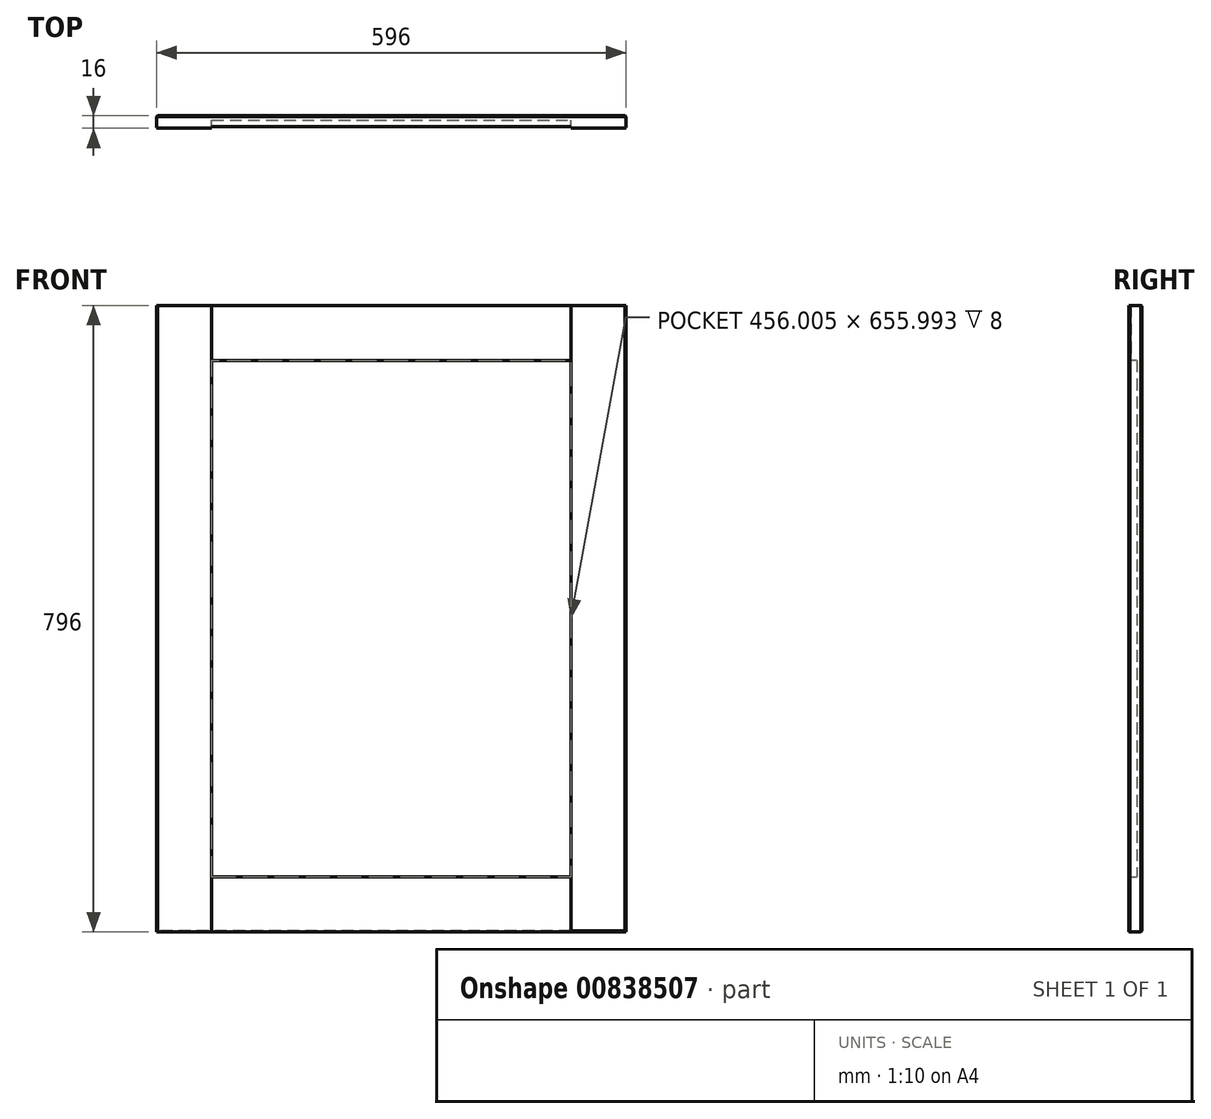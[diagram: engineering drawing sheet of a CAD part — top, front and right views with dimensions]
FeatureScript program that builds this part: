
annotation { "Feature Type Name" : "Feature", "Feature Type Description" : "" }
export const myFeature = defineFeature(function(context is Context, id is Id, definition is map)
    precondition{}
    {
        {
            var Q0;
            Q0=qCreatedBy(makeId("Front.planeOp"),FACE);
            var sketch = newSketch(context, id + "F0", { "sketchPlane" : qUnion([Q0])});
            skLineSegment(sketch, "E0.bottom", {"start": v(0, 0) * mm, "end": v(35.9, 0) * mm});
            skLineSegment(sketch, "E0.top", {"start": v(0, 30.12) * mm, "end": v(35.9, 30.12) * mm});
            skLineSegment(sketch, "E0.left", {"start": v(0, 0) * mm, "end": v(0, 30.12) * mm});
            skLineSegment(sketch, "E0.right", {"start": v(35.9, 0) * mm, "end": v(35.9, 30.12) * mm});
            skSolve(sketch);
        }
        {
            var Q0;
            Q0=makeQuery(id+"F0.imprint","IMPRINT",FACE,{"disambiguationData":[TD([[makeQuery(id+"F0.imprint","IMPRINT",EDGE,{"derivedFrom":sQuery(id+"F0.wireOp",EDGE,"E0.bottom")}),1.0]])]});
            extrude(context, id + "F1", {"entities" : qUnion([Q0]), "depth" : 16 * mm, "offsetDistance" : 25.4 * mm});
        }
        {
            var Q0;
            Q0=makeQuery(id+"F1.opExtrude","SWEPT_FACE",FACE,{"disambiguationData":[OSD([sQuery(id+"F0.wireOp",EDGE,"E0.left")])]});
            extrude(context, id + "F2", {"entities" : qUnion([Q0]), "operationType" : NewBodyOperationType.ADD, "oppositeDirection" : true, "depth" : 196 * mm, "offsetDistance" : 25 * mm});
        }
        {
            var Q0;
            {var subQ0=sQuery(id+"F0.wireOp",EDGE,"E0.bottom");Q0=makeQuery(id+"F2.boolean.opBoolean","MERGE",FACE,{"derivedFrom":[makeQuery(id+"F1.opExtrude","SWEPT_FACE",FACE,{"disambiguationData":[OSD([subQ0])]}),makeQuery(id+"F2.opExtrude","SWEPT_FACE",FACE,{"disambiguationData":[OSD([subQ0,sQuery(id+"F0.wireOp",EDGE,"E0.left")])]})]});}
            extrude(context, id + "F3", {"entities" : qUnion([Q0]), "operationType" : NewBodyOperationType.ADD, "oppositeDirection" : true, "depth" : 796 * mm, "offsetDistance" : 25 * mm});
        }
        {
            var Q0;
            {var subQ0=sQuery(id+"F0.wireOp",EDGE,"E0.left");var subQ1=sQuery(id+"F0.wireOp",EDGE,"E0.bottom");Q0=makeQuery(id+"F3.boolean.opBoolean","MERGE",FACE,{"derivedFrom":[makeQuery(id+"F2.boolean.opBoolean","MERGE",FACE,{"derivedFrom":[makeQuery(id+"F1.opExtrude","CAP_FACE",FACE,{"disambiguationData":[OSD([subQ1,sQuery(id+"F0.wireOp",EDGE,"E0.top"),subQ0,sQuery(id+"F0.wireOp",EDGE,"E0.right")])],"isStart":false}),makeQuery(id+"F2.opExtrude","SWEPT_FACE",FACE,{"disambiguationData":[OSD([subQ0]),TDD([makeQuery(id+"F1.opExtrude","CAP_EDGE",EDGE,{"disambiguationData":[OSD([subQ0])],"isStart":false})])]})]}),makeQuery(id+"F3.opExtrude","SWEPT_FACE",FACE,{"disambiguationData":[OSD([subQ1,subQ0]),TDD([makeQuery(id+"F2.boolean.opBoolean","MERGE",EDGE,{"derivedFrom":[makeQuery(id+"F1.opExtrude","CAP_EDGE",EDGE,{"disambiguationData":[OSD([subQ1])],"isStart":false}),makeQuery(id+"F2.opExtrude","SWEPT_EDGE",EDGE,{"disambiguationData":[OSD([subQ1,subQ0]),TDD([makeQuery(id+"F1.opExtrude","CAP_VERTEX",VERTEX,{"disambiguationData":[OSD([subQ1,subQ0])],"isStart":false})])]})]})])]})]});}
            var sketch = newSketch(context, id + "F4", { "sketchPlane" : qUnion([Q0])});
            skLineSegment(sketch, "E1.bottom", {"start": v(0, 796) * mm, "end": v(42.19, 796) * mm});
            skLineSegment(sketch, "E1.top", {"start": v(0, 751.57) * mm, "end": v(42.19, 751.57) * mm});
            skLineSegment(sketch, "E1.left", {"start": v(0, 796) * mm, "end": v(0, 751.57) * mm});
            skLineSegment(sketch, "E1.right", {"start": v(42.19, 796) * mm, "end": v(42.19, 751.57) * mm});
            skLineSegment(sketch, "E2.bottom", {"start": v(196, 796) * mm, "end": v(153.6, 796) * mm});
            skLineSegment(sketch, "E2.top", {"start": v(196, 746.75) * mm, "end": v(153.6, 746.75) * mm});
            skLineSegment(sketch, "E2.left", {"start": v(196, 796) * mm, "end": v(196, 746.75) * mm});
            skLineSegment(sketch, "E2.right", {"start": v(153.6, 796) * mm, "end": v(153.6, 746.75) * mm});
            skSolve(sketch);
        }
        {
            var Q0;
            Q0=makeQuery(id+"F4.imprint","IMPRINT",FACE,{"disambiguationData":[TD([[makeQuery(id+"F4.imprint","IMPRINT",EDGE,{"derivedFrom":sQuery(id+"F4.wireOp",EDGE,"E1.bottom")}),-1.0]])]});
            var Q1;
            Q1=makeQuery(id+"F4.imprint","IMPRINT",FACE,{"disambiguationData":[TD([[makeQuery(id+"F4.imprint","IMPRINT",EDGE,{"derivedFrom":sQuery(id+"F4.wireOp",EDGE,"E2.bottom")}),-1.0]])]});
            extrude(context, id + "F5", {"entities" : qUnion([Q0, Q1]), "operationType" : NewBodyOperationType.ADD, "depth" : 25 * mm, "offsetDistance" : 25 * mm});
        }
        {
            var Q0;
            {var subQ0=sQuery(id+"F0.wireOp",EDGE,"E0.left");var subQ1=sQuery(id+"F0.wireOp",EDGE,"E0.bottom");Q0=makeQuery(id+"F3.boolean.opBoolean","MERGE",FACE,{"derivedFrom":[makeQuery(id+"F2.boolean.opBoolean","MERGE",FACE,{"derivedFrom":[makeQuery(id+"F1.opExtrude","CAP_FACE",FACE,{"disambiguationData":[OSD([subQ1,sQuery(id+"F0.wireOp",EDGE,"E0.top"),subQ0,sQuery(id+"F0.wireOp",EDGE,"E0.right")])],"isStart":false}),makeQuery(id+"F2.opExtrude","SWEPT_FACE",FACE,{"disambiguationData":[OSD([subQ0]),TDD([makeQuery(id+"F1.opExtrude","CAP_EDGE",EDGE,{"disambiguationData":[OSD([subQ0])],"isStart":false})])]})]}),makeQuery(id+"F3.opExtrude","SWEPT_FACE",FACE,{"disambiguationData":[OSD([subQ1,subQ0]),TDD([makeQuery(id+"F2.boolean.opBoolean","MERGE",EDGE,{"derivedFrom":[makeQuery(id+"F1.opExtrude","CAP_EDGE",EDGE,{"disambiguationData":[OSD([subQ1])],"isStart":false}),makeQuery(id+"F2.opExtrude","SWEPT_EDGE",EDGE,{"disambiguationData":[OSD([subQ1,subQ0]),TDD([makeQuery(id+"F1.opExtrude","CAP_VERTEX",VERTEX,{"disambiguationData":[OSD([subQ1,subQ0])],"isStart":false})])]})]})])]})]});}
            var sketch = newSketch(context, id + "F6", { "sketchPlane" : qUnion([Q0])});
            skLineSegment(sketch, "E3.bottom", {"start": v(196, 0) * mm, "end": v(163.38, 0) * mm});
            skLineSegment(sketch, "E3.top", {"start": v(196, 46.55) * mm, "end": v(163.38, 46.55) * mm});
            skLineSegment(sketch, "E3.left", {"start": v(196, 0) * mm, "end": v(196, 46.55) * mm});
            skLineSegment(sketch, "E3.right", {"start": v(163.38, 0) * mm, "end": v(163.38, 46.55) * mm});
            skLineSegment(sketch, "E4.bottom", {"start": v(0, 0) * mm, "end": v(50.28, 0) * mm});
            skLineSegment(sketch, "E4.top", {"start": v(0, 44.4) * mm, "end": v(50.28, 44.4) * mm});
            skLineSegment(sketch, "E4.left", {"start": v(0, 0) * mm, "end": v(0, 44.4) * mm});
            skLineSegment(sketch, "E4.right", {"start": v(50.28, 0) * mm, "end": v(50.28, 44.4) * mm});
            skSolve(sketch);
        }
        {
            var Q0;
            Q0=makeQuery(id+"F6.imprint","IMPRINT",FACE,{"disambiguationData":[TD([[makeQuery(id+"F6.imprint","IMPRINT",EDGE,{"derivedFrom":sQuery(id+"F6.wireOp",EDGE,"E3.bottom")}),1.0]])]});
            var Q1;
            Q1=makeQuery(id+"F6.imprint","IMPRINT",FACE,{"disambiguationData":[TD([[makeQuery(id+"F6.imprint","IMPRINT",EDGE,{"derivedFrom":sQuery(id+"F6.wireOp",EDGE,"E4.bottom")}),1.0]])]});
            extrude(context, id + "F7", {"entities" : qUnion([Q0, Q1]), "operationType" : NewBodyOperationType.ADD, "depth" : 25 * mm, "offsetDistance" : 25 * mm});
        }
        {
            var Q0;
            Q0=makeQuery(id+"F7.opExtrude","SWEPT_FACE",FACE,{"disambiguationData":[OSD([sQuery(id+"F6.wireOp",EDGE,"E4.right")])]});
            extrude(context, id + "F8", {"entities" : qUnion([Q0]), "operationType" : NewBodyOperationType.ADD, "depth" : 19.72 * mm, "offsetDistance" : 25 * mm});
        }
        {
            var Q0;
            {var subQ0=sQuery(id+"F6.wireOp",EDGE,"E4.top");Q0=makeQuery(id+"F8.boolean.opBoolean","MERGE",FACE,{"derivedFrom":[makeQuery(id+"F7.opExtrude","SWEPT_FACE",FACE,{"disambiguationData":[OSD([subQ0])]}),makeQuery(id+"F8.opExtrude","SWEPT_FACE",FACE,{"disambiguationData":[OSD([subQ0,sQuery(id+"F6.wireOp",EDGE,"E4.right")])]})]});}
            extrude(context, id + "F9", {"entities" : qUnion([Q0]), "operationType" : NewBodyOperationType.ADD, "depth" : 25.6 * mm, "offsetDistance" : 25 * mm});
        }
        {
            var Q0;
            Q0=makeQuery(id+"F7.opExtrude","SWEPT_FACE",FACE,{"disambiguationData":[OSD([sQuery(id+"F6.wireOp",EDGE,"E3.right")])]});
            extrude(context, id + "F10", {"entities" : qUnion([Q0]), "operationType" : NewBodyOperationType.ADD, "depth" : 37.38 * mm, "offsetDistance" : 25 * mm});
        }
        {
            var Q0;
            {var subQ0=sQuery(id+"F6.wireOp",EDGE,"E3.top");Q0=makeQuery(id+"F10.boolean.opBoolean","MERGE",FACE,{"derivedFrom":[makeQuery(id+"F7.opExtrude","SWEPT_FACE",FACE,{"disambiguationData":[OSD([subQ0])]}),makeQuery(id+"F10.opExtrude","SWEPT_FACE",FACE,{"disambiguationData":[OSD([subQ0,sQuery(id+"F6.wireOp",EDGE,"E3.right")])]})]});}
            extrude(context, id + "F11", {"entities" : qUnion([Q0]), "operationType" : NewBodyOperationType.ADD, "depth" : 23.45 * mm, "offsetDistance" : 25 * mm});
        }
        {
            var Q0;
            Q0=makeQuery(id+"F5.opExtrude","SWEPT_FACE",FACE,{"disambiguationData":[OSD([sQuery(id+"F4.wireOp",EDGE,"E1.right")])]});
            extrude(context, id + "F12", {"entities" : qUnion([Q0]), "operationType" : NewBodyOperationType.ADD, "depth" : 27.8 * mm, "offsetDistance" : 25 * mm});
        }
        {
            var Q0;
            {var subQ0=sQuery(id+"F4.wireOp",EDGE,"E1.top");Q0=makeQuery(id+"F12.boolean.opBoolean","MERGE",FACE,{"derivedFrom":[makeQuery(id+"F5.opExtrude","SWEPT_FACE",FACE,{"disambiguationData":[OSD([subQ0])]}),makeQuery(id+"F12.opExtrude","SWEPT_FACE",FACE,{"disambiguationData":[OSD([subQ0,sQuery(id+"F4.wireOp",EDGE,"E1.right")])]})]});}
            extrude(context, id + "F13", {"entities" : qUnion([Q0]), "operationType" : NewBodyOperationType.ADD, "depth" : 25.57 * mm, "offsetDistance" : 25 * mm});
        }
        {
            var Q0;
            Q0=makeQuery(id+"F5.opExtrude","SWEPT_FACE",FACE,{"disambiguationData":[OSD([sQuery(id+"F4.wireOp",EDGE,"E2.top")])]});
            extrude(context, id + "F14", {"entities" : qUnion([Q0]), "operationType" : NewBodyOperationType.ADD, "depth" : 20.75 * mm, "offsetDistance" : 25 * mm});
        }
        {
            var Q0;
            {var subQ0=sQuery(id+"F4.wireOp",EDGE,"E2.right");Q0=makeQuery(id+"F14.boolean.opBoolean","MERGE",FACE,{"derivedFrom":[makeQuery(id+"F5.opExtrude","SWEPT_FACE",FACE,{"disambiguationData":[OSD([subQ0])]}),makeQuery(id+"F14.opExtrude","SWEPT_FACE",FACE,{"disambiguationData":[OSD([sQuery(id+"F4.wireOp",EDGE,"E2.top"),subQ0])]})]});}
            extrude(context, id + "F15", {"entities" : qUnion([Q0]), "operationType" : NewBodyOperationType.ADD, "depth" : 27.6 * mm, "offsetDistance" : 25 * mm});
        }
        {
            var Q0;
            {var subQ0=sQuery(id+"F0.wireOp",EDGE,"E0.left");var subQ1=sQuery(id+"F0.wireOp",EDGE,"E0.bottom");Q0=makeQuery(id+"F3.boolean.opBoolean","MERGE",FACE,{"derivedFrom":[makeQuery(id+"F2.boolean.opBoolean","MERGE",FACE,{"derivedFrom":[makeQuery(id+"F1.opExtrude","CAP_FACE",FACE,{"disambiguationData":[OSD([subQ1,sQuery(id+"F0.wireOp",EDGE,"E0.top"),subQ0,sQuery(id+"F0.wireOp",EDGE,"E0.right")])],"isStart":false}),makeQuery(id+"F2.opExtrude","SWEPT_FACE",FACE,{"disambiguationData":[OSD([subQ0]),TDD([makeQuery(id+"F1.opExtrude","CAP_EDGE",EDGE,{"disambiguationData":[OSD([subQ0])],"isStart":false})])]})]}),makeQuery(id+"F3.opExtrude","SWEPT_FACE",FACE,{"disambiguationData":[OSD([subQ1,subQ0]),TDD([makeQuery(id+"F2.boolean.opBoolean","MERGE",EDGE,{"derivedFrom":[makeQuery(id+"F1.opExtrude","CAP_EDGE",EDGE,{"disambiguationData":[OSD([subQ1])],"isStart":false}),makeQuery(id+"F2.opExtrude","SWEPT_EDGE",EDGE,{"disambiguationData":[OSD([subQ1,subQ0]),TDD([makeQuery(id+"F1.opExtrude","CAP_VERTEX",VERTEX,{"disambiguationData":[OSD([subQ1,subQ0])],"isStart":false})])]})]})])]})]});}
            var sketch = newSketch(context, id + "F16", { "sketchPlane" : qUnion([Q0])});
            skLineSegment(sketch, "E5.bottom", {"start": v(70, 726) * mm, "end": v(126, 726) * mm});
            skLineSegment(sketch, "E5.top", {"start": v(70, 70) * mm, "end": v(126, 70) * mm});
            skLineSegment(sketch, "E5.left", {"start": v(70, 726) * mm, "end": v(70, 70) * mm});
            skLineSegment(sketch, "E5.right", {"start": v(126, 726) * mm, "end": v(126, 70) * mm});
            skSolve(sketch);
        }
        {
            var Q0;
            Q0=makeQuery(id+"F16.imprint","IMPRINT",FACE,{"disambiguationData":[TD([[makeQuery(id+"F16.imprint","IMPRINT",EDGE,{"derivedFrom":sQuery(id+"F16.wireOp",EDGE,"E5.top")}),1.0]])]});
            extrude(context, id + "F17", {"entities" : qUnion([Q0]), "operationType" : NewBodyOperationType.REMOVE, "oppositeDirection" : true, "depth" : 10 * mm, "offsetDistance" : 25 * mm});
        }
        {
            var Q0;
            {var subQ2=sQuery(id+"F0.wireOp",EDGE,"E0.left");var subQ3=sQuery(id+"F0.wireOp",EDGE,"E0.bottom");var subQ4=makeQuery(id+"F1.opExtrude","CAP_FACE",FACE,{"disambiguationData":[OSD([subQ3,sQuery(id+"F0.wireOp",EDGE,"E0.top"),subQ2,sQuery(id+"F0.wireOp",EDGE,"E0.right")])],"isStart":false});var subQ7=makeQuery(id+"F3.opExtrude","SWEPT_FACE",FACE,{"disambiguationData":[OSD([subQ3,subQ2]),TDD([makeQuery(id+"F2.boolean.opBoolean","MERGE",EDGE,{"derivedFrom":[makeQuery(id+"F1.opExtrude","CAP_EDGE",EDGE,{"disambiguationData":[OSD([subQ3])],"isStart":false}),makeQuery(id+"F2.opExtrude","SWEPT_EDGE",EDGE,{"disambiguationData":[OSD([subQ3,subQ2]),TDD([makeQuery(id+"F1.opExtrude","CAP_VERTEX",VERTEX,{"disambiguationData":[OSD([subQ3,subQ2])],"isStart":false})])]})]})])]});var subQ8=makeQuery(id+"F2.opExtrude","SWEPT_FACE",FACE,{"disambiguationData":[OSD([subQ2]),TDD([makeQuery(id+"F1.opExtrude","CAP_EDGE",EDGE,{"disambiguationData":[OSD([subQ2])],"isStart":false})])]});Q0=makeQuery(id+"F17.boolean.opBoolean","SPLIT",FACE,{"disambiguationData":[TD([makeQuery(id+"F1.opExtrude","SWEPT_FACE",FACE,{"disambiguationData":[OSD([subQ3])]})])],"derivedFrom":makeQuery(id+"F3.boolean.opBoolean","MERGE",FACE,{"derivedFrom":[makeQuery(id+"F2.boolean.opBoolean","MERGE",FACE,{"derivedFrom":[subQ4,subQ8]}),subQ7]})});}
            var Q1;
            {var subQ2=sQuery(id+"F4.wireOp",EDGE,"E1.bottom");var subQ3=sQuery(id+"F0.wireOp",EDGE,"E0.left");var subQ4=sQuery(id+"F0.wireOp",EDGE,"E0.bottom");var subQ6=makeQuery(id+"F1.opExtrude","CAP_FACE",FACE,{"disambiguationData":[OSD([subQ4,sQuery(id+"F0.wireOp",EDGE,"E0.top"),subQ3,sQuery(id+"F0.wireOp",EDGE,"E0.right")])],"isStart":false});var subQ7=makeQuery(id+"F2.opExtrude","SWEPT_FACE",FACE,{"disambiguationData":[OSD([subQ3]),TDD([makeQuery(id+"F1.opExtrude","CAP_EDGE",EDGE,{"disambiguationData":[OSD([subQ3])],"isStart":false})])]});var subQ8=makeQuery(id+"F3.opExtrude","SWEPT_FACE",FACE,{"disambiguationData":[OSD([subQ4,subQ3]),TDD([makeQuery(id+"F2.boolean.opBoolean","MERGE",EDGE,{"derivedFrom":[makeQuery(id+"F1.opExtrude","CAP_EDGE",EDGE,{"disambiguationData":[OSD([subQ4])],"isStart":false}),makeQuery(id+"F2.opExtrude","SWEPT_EDGE",EDGE,{"disambiguationData":[OSD([subQ4,subQ3]),TDD([makeQuery(id+"F1.opExtrude","CAP_VERTEX",VERTEX,{"disambiguationData":[OSD([subQ4,subQ3])],"isStart":false})])]})]})])]});Q1=makeQuery(id+"F17.boolean.opBoolean","SPLIT",FACE,{"disambiguationData":[TD([makeQuery(id+"F5.opExtrude","SWEPT_FACE",FACE,{"disambiguationData":[OSD([subQ2])]})])],"derivedFrom":makeQuery(id+"F3.boolean.opBoolean","MERGE",FACE,{"derivedFrom":[makeQuery(id+"F2.boolean.opBoolean","MERGE",FACE,{"derivedFrom":[subQ6,subQ7]}),subQ8]})});}
            extrude(context, id + "F18", {"entities" : qUnion([Q0, Q1]), "operationType" : NewBodyOperationType.REMOVE, "oppositeDirection" : true, "depth" : 2 * mm, "offsetDistance" : 25 * mm});
        }
        {
            var Q0;
            {var subQ0=sQuery(id+"F4.wireOp",EDGE,"E1.right");var subQ1=sQuery(id+"F4.wireOp",EDGE,"E1.top");Q0=makeQuery(id+"F13.boolean.opBoolean","MERGE",FACE,{"derivedFrom":[makeQuery(id+"F12.boolean.opBoolean","MERGE",FACE,{"derivedFrom":[makeQuery(id+"F5.opExtrude","CAP_FACE",FACE,{"disambiguationData":[OSD([sQuery(id+"F4.wireOp",EDGE,"E1.bottom"),subQ1,sQuery(id+"F4.wireOp",EDGE,"E1.left"),subQ0])],"isStart":false}),makeQuery(id+"F12.opExtrude","SWEPT_FACE",FACE,{"disambiguationData":[OSD([subQ0]),TDD([makeQuery(id+"F5.opExtrude","CAP_EDGE",EDGE,{"disambiguationData":[OSD([subQ0])],"isStart":false})])]})]}),makeQuery(id+"F13.opExtrude","SWEPT_FACE",FACE,{"disambiguationData":[OSD([subQ1,subQ0]),TDD([makeQuery(id+"F12.boolean.opBoolean","MERGE",EDGE,{"derivedFrom":[makeQuery(id+"F5.opExtrude","CAP_EDGE",EDGE,{"disambiguationData":[OSD([subQ1])],"isStart":false}),makeQuery(id+"F12.opExtrude","SWEPT_EDGE",EDGE,{"disambiguationData":[OSD([subQ1,subQ0]),TDD([makeQuery(id+"F5.opExtrude","CAP_VERTEX",VERTEX,{"disambiguationData":[OSD([subQ1,subQ0])],"isStart":false})])]})]})])]})]});}
            var Q1;
            {var subQ0=sQuery(id+"F4.wireOp",EDGE,"E2.right");var subQ1=sQuery(id+"F4.wireOp",EDGE,"E2.top");Q1=makeQuery(id+"F15.boolean.opBoolean","MERGE",FACE,{"derivedFrom":[makeQuery(id+"F14.boolean.opBoolean","MERGE",FACE,{"derivedFrom":[makeQuery(id+"F5.opExtrude","CAP_FACE",FACE,{"disambiguationData":[OSD([sQuery(id+"F4.wireOp",EDGE,"E2.bottom"),subQ1,sQuery(id+"F4.wireOp",EDGE,"E2.left"),subQ0])],"isStart":false}),makeQuery(id+"F14.opExtrude","SWEPT_FACE",FACE,{"disambiguationData":[OSD([subQ1]),TDD([makeQuery(id+"F5.opExtrude","CAP_EDGE",EDGE,{"disambiguationData":[OSD([subQ1])],"isStart":false})])]})]}),makeQuery(id+"F15.opExtrude","SWEPT_FACE",FACE,{"disambiguationData":[OSD([subQ1,subQ0]),TDD([makeQuery(id+"F14.boolean.opBoolean","MERGE",EDGE,{"derivedFrom":[makeQuery(id+"F5.opExtrude","CAP_EDGE",EDGE,{"disambiguationData":[OSD([subQ0])],"isStart":false}),makeQuery(id+"F14.opExtrude","SWEPT_EDGE",EDGE,{"disambiguationData":[OSD([subQ1,subQ0]),TDD([makeQuery(id+"F5.opExtrude","CAP_VERTEX",VERTEX,{"disambiguationData":[OSD([subQ1,subQ0])],"isStart":false})])]})]})])]})]});}
            var Q2;
            {var subQ0=sQuery(id+"F6.wireOp",EDGE,"E4.right");var subQ1=sQuery(id+"F6.wireOp",EDGE,"E4.top");Q2=makeQuery(id+"F9.boolean.opBoolean","MERGE",FACE,{"derivedFrom":[makeQuery(id+"F8.boolean.opBoolean","MERGE",FACE,{"derivedFrom":[makeQuery(id+"F7.opExtrude","CAP_FACE",FACE,{"disambiguationData":[OSD([sQuery(id+"F6.wireOp",EDGE,"E4.bottom"),subQ1,sQuery(id+"F6.wireOp",EDGE,"E4.left"),subQ0])],"isStart":false}),makeQuery(id+"F8.opExtrude","SWEPT_FACE",FACE,{"disambiguationData":[OSD([subQ0]),TDD([makeQuery(id+"F7.opExtrude","CAP_EDGE",EDGE,{"disambiguationData":[OSD([subQ0])],"isStart":false})])]})]}),makeQuery(id+"F9.opExtrude","SWEPT_FACE",FACE,{"disambiguationData":[OSD([subQ1,subQ0]),TDD([makeQuery(id+"F8.boolean.opBoolean","MERGE",EDGE,{"derivedFrom":[makeQuery(id+"F7.opExtrude","CAP_EDGE",EDGE,{"disambiguationData":[OSD([subQ1])],"isStart":false}),makeQuery(id+"F8.opExtrude","SWEPT_EDGE",EDGE,{"disambiguationData":[OSD([subQ1,subQ0]),TDD([makeQuery(id+"F7.opExtrude","CAP_VERTEX",VERTEX,{"disambiguationData":[OSD([subQ1,subQ0])],"isStart":false})])]})]})])]})]});}
            var Q3;
            {var subQ0=sQuery(id+"F6.wireOp",EDGE,"E3.right");var subQ1=sQuery(id+"F6.wireOp",EDGE,"E3.top");Q3=makeQuery(id+"F11.boolean.opBoolean","MERGE",FACE,{"derivedFrom":[makeQuery(id+"F10.boolean.opBoolean","MERGE",FACE,{"derivedFrom":[makeQuery(id+"F7.opExtrude","CAP_FACE",FACE,{"disambiguationData":[OSD([sQuery(id+"F6.wireOp",EDGE,"E3.bottom"),subQ1,sQuery(id+"F6.wireOp",EDGE,"E3.left"),subQ0])],"isStart":false}),makeQuery(id+"F10.opExtrude","SWEPT_FACE",FACE,{"disambiguationData":[OSD([subQ0]),TDD([makeQuery(id+"F7.opExtrude","CAP_EDGE",EDGE,{"disambiguationData":[OSD([subQ0])],"isStart":false})])]})]}),makeQuery(id+"F11.opExtrude","SWEPT_FACE",FACE,{"disambiguationData":[OSD([subQ1,subQ0]),TDD([makeQuery(id+"F10.boolean.opBoolean","MERGE",EDGE,{"derivedFrom":[makeQuery(id+"F7.opExtrude","CAP_EDGE",EDGE,{"disambiguationData":[OSD([subQ1])],"isStart":false}),makeQuery(id+"F10.opExtrude","SWEPT_EDGE",EDGE,{"disambiguationData":[OSD([subQ1,subQ0]),TDD([makeQuery(id+"F7.opExtrude","CAP_VERTEX",VERTEX,{"disambiguationData":[OSD([subQ1,subQ0])],"isStart":false})])]})]})])]})]});}
            extrude(context, id + "F19", {"entities" : qUnion([Q0, Q1, Q2, Q3]), "operationType" : NewBodyOperationType.REMOVE, "oppositeDirection" : true, "depth" : 25 * mm, "offsetDistance" : 25 * mm});
        }
        {
            var Q0;
            {var subQ0=sQuery(id+"F4.wireOp",EDGE,"E2.left");var subQ1=sQuery(id+"F0.wireOp",EDGE,"E0.left");var subQ2=sQuery(id+"F0.wireOp",EDGE,"E0.bottom");var subQ3=sQuery(id+"F6.wireOp",EDGE,"E3.left");Q0=makeQuery(id+"F14.boolean.opBoolean","MERGE",FACE,{"derivedFrom":[makeQuery(id+"F11.boolean.opBoolean","MERGE",FACE,{"derivedFrom":[makeQuery(id+"F7.boolean.opBoolean","MERGE",FACE,{"derivedFrom":[makeQuery(id+"F5.boolean.opBoolean","MERGE",FACE,{"derivedFrom":[makeQuery(id+"F3.boolean.opBoolean","MERGE",FACE,{"derivedFrom":[makeQuery(id+"F2.opExtrude","CAP_FACE",FACE,{"disambiguationData":[OSD([subQ1])],"isStart":false}),makeQuery(id+"F3.opExtrude","SWEPT_FACE",FACE,{"disambiguationData":[OSD([subQ2,subQ1]),TDD([makeQuery(id+"F2.opExtrude","CAP_EDGE",EDGE,{"disambiguationData":[OSD([subQ2,subQ1])],"isStart":false})])]})]}),makeQuery(id+"F5.opExtrude","SWEPT_FACE",FACE,{"disambiguationData":[OSD([subQ0])]})]}),makeQuery(id+"F7.opExtrude","SWEPT_FACE",FACE,{"disambiguationData":[OSD([subQ3])]})]}),makeQuery(id+"F11.opExtrude","SWEPT_FACE",FACE,{"disambiguationData":[OSD([subQ2,subQ1,sQuery(id+"F6.wireOp",EDGE,"E3.top"),subQ3])]})]}),makeQuery(id+"F14.opExtrude","SWEPT_FACE",FACE,{"disambiguationData":[OSD([subQ2,subQ1,sQuery(id+"F4.wireOp",EDGE,"E2.top"),subQ0])]})]});}
            extrude(context, id + "F20", {"entities" : qUnion([Q0]), "operationType" : NewBodyOperationType.ADD, "depth" : 400 * mm, "offsetDistance" : 25 * mm});
        }
        {
            var Q0;
            {var subQ0=sQuery(id+"F6.wireOp",EDGE,"E3.right");var subQ1=sQuery(id+"F6.wireOp",EDGE,"E3.top");Q0=makeQuery(id+"F18.boolean.opBoolean","MERGE",FACE,{"derivedFrom":[makeQuery(id+"F11.boolean.opBoolean","MERGE",FACE,{"derivedFrom":[makeQuery(id+"F10.opExtrude","CAP_FACE",FACE,{"disambiguationData":[OSD([subQ0])],"isStart":false}),makeQuery(id+"F11.opExtrude","SWEPT_FACE",FACE,{"disambiguationData":[OSD([subQ1,subQ0]),TDD([makeQuery(id+"F10.opExtrude","CAP_EDGE",EDGE,{"disambiguationData":[OSD([subQ1,subQ0])],"isStart":false})])]})]}),makeQuery(id+"F17.boolean.opBoolean","COPY",FACE,{"derivedFrom":makeQuery(id+"F17.opExtrude","SWEPT_FACE",FACE,{"disambiguationData":[OSD([sQuery(id+"F16.wireOp",EDGE,"E5.right")])]})}),makeQuery(id+"F18.opExtrude","SWEPT_FACE",FACE,{"disambiguationData":[OSD([subQ1,subQ0])]})]});}
            var Q1;
            {var subQ0=sQuery(id+"F4.wireOp",EDGE,"E2.right");var subQ1=sQuery(id+"F4.wireOp",EDGE,"E2.top");Q1=makeQuery(id+"F18.boolean.opBoolean","MERGE",FACE,{"derivedFrom":[makeQuery(id+"F15.opExtrude","CAP_FACE",FACE,{"disambiguationData":[OSD([subQ1,subQ0])],"isStart":false}),makeQuery(id+"F18.opExtrude","SWEPT_FACE",FACE,{"disambiguationData":[OSD([subQ1,subQ0])]})]});}
            extrude(context, id + "F21", {"entities" : qUnion([Q0, Q1]), "operationType" : NewBodyOperationType.REMOVE, "oppositeDirection" : true, "depth" : 400 * mm, "offsetDistance" : 25 * mm});
        }
        {
            var Q0;
            {var subQ0=sQuery(id+"F4.wireOp",EDGE,"E2.bottom");var subQ1=sQuery(id+"F0.wireOp",EDGE,"E0.left");var subQ2=sQuery(id+"F0.wireOp",EDGE,"E0.bottom");var subQ3=sQuery(id+"F4.wireOp",EDGE,"E1.bottom");Q0=makeQuery(id+"F20.boolean.opBoolean","MERGE",FACE,{"derivedFrom":[makeQuery(id+"F15.boolean.opBoolean","MERGE",FACE,{"derivedFrom":[makeQuery(id+"F12.boolean.opBoolean","MERGE",FACE,{"derivedFrom":[makeQuery(id+"F5.boolean.opBoolean","MERGE",FACE,{"derivedFrom":[makeQuery(id+"F3.opExtrude","CAP_FACE",FACE,{"disambiguationData":[OSD([subQ2,subQ1])],"isStart":false}),makeQuery(id+"F5.opExtrude","SWEPT_FACE",FACE,{"disambiguationData":[OSD([subQ3])]}),makeQuery(id+"F5.opExtrude","SWEPT_FACE",FACE,{"disambiguationData":[OSD([subQ0])]})]}),makeQuery(id+"F12.opExtrude","SWEPT_FACE",FACE,{"disambiguationData":[OSD([subQ2,subQ1,subQ3,sQuery(id+"F4.wireOp",EDGE,"E1.right")])]})]}),makeQuery(id+"F15.opExtrude","SWEPT_FACE",FACE,{"disambiguationData":[OSD([subQ2,subQ1,subQ0,sQuery(id+"F4.wireOp",EDGE,"E2.right")])]})]}),makeQuery(id+"F20.opExtrude","SWEPT_FACE",FACE,{"disambiguationData":[OSD([subQ2,subQ1,subQ0,sQuery(id+"F4.wireOp",EDGE,"E2.left")])]})]});}
            extrude(context, id + "F22", {"entities" : qUnion([Q0]), "operationType" : NewBodyOperationType.ADD, "depth" : 200 * mm, "offsetDistance" : 25 * mm});
        }
        {
            var Q0;
            Q0=makeQuery(id+"F17.boolean.opBoolean","COPY",FACE,{"derivedFrom":makeQuery(id+"F17.opExtrude","SWEPT_FACE",FACE,{"disambiguationData":[OSD([sQuery(id+"F16.wireOp",EDGE,"E5.bottom")])]})});
            var Q1;
            {var subQ0=sQuery(id+"F16.wireOp",EDGE,"E5.right");var subQ1=sQuery(id+"F16.wireOp",EDGE,"E5.bottom");var subQ2=sQuery(id+"F4.wireOp",EDGE,"E2.right");var subQ3=sQuery(id+"F4.wireOp",EDGE,"E2.top");var subQ4=makeQuery(id+"F17.boolean.opBoolean","COPY",EDGE,{"derivedFrom":makeQuery(id+"F17.opExtrude","SWEPT_EDGE",EDGE,{"disambiguationData":[OSD([subQ3,subQ2,subQ1,subQ0])]})});Q1=makeQuery(id+"F21.boolean.opBoolean","COPY",FACE,{"derivedFrom":makeQuery(id+"F21.opExtrude","SWEPT_FACE",FACE,{"disambiguationData":[OSD([subQ3,subQ2,subQ1,subQ0]),TDD([makeQuery(id+"F18.boolean.opBoolean","MERGE",EDGE,{"derivedFrom":[subQ4,makeQuery(id+"F18.opExtrude","SWEPT_EDGE",EDGE,{"disambiguationData":[OSD([subQ3,subQ2,subQ1,subQ0])]})]}),makeQuery(id+"F18.boolean.opBoolean","SPLIT",EDGE,{"derivedFrom":subQ4})])]})});}
            extrude(context, id + "F23", {"entities" : qUnion([Q0, Q1]), "operationType" : NewBodyOperationType.REMOVE, "oppositeDirection" : true, "depth" : 200 * mm, "offsetDistance" : 25 * mm});
        }
        {
            var Q0;
            Q0=makeQuery(id+"F23.boolean.opBoolean","COPY",FACE,{"derivedFrom":makeQuery(id+"F23.opExtrude","CAP_FACE",FACE,{"disambiguationData":[OSD([sQuery(id+"F4.wireOp",EDGE,"E2.top"),sQuery(id+"F4.wireOp",EDGE,"E2.right"),sQuery(id+"F16.wireOp",EDGE,"E5.bottom"),sQuery(id+"F16.wireOp",EDGE,"E5.right")])],"isStart":false})});
            var Q1;
            Q1=makeQuery(id+"F23.boolean.opBoolean","COPY",FACE,{"derivedFrom":makeQuery(id+"F23.opExtrude","CAP_FACE",FACE,{"disambiguationData":[OSD([sQuery(id+"F16.wireOp",EDGE,"E5.bottom")])],"isStart":false})});
            extrude(context, id + "F24", {"entities" : qUnion([Q0, Q1]), "operationType" : NewBodyOperationType.ADD, "depth" : 200 * mm, "offsetDistance" : 25 * mm});
        }
        {
            var Q0;
            Q0=makeQuery(id+"F22.opExtrude","CAP_FACE",FACE,{"disambiguationData":[OSD([sQuery(id+"F0.wireOp",EDGE,"E0.bottom"),sQuery(id+"F0.wireOp",EDGE,"E0.left"),sQuery(id+"F4.wireOp",EDGE,"E1.bottom"),sQuery(id+"F4.wireOp",EDGE,"E1.right"),sQuery(id+"F4.wireOp",EDGE,"E2.bottom"),sQuery(id+"F4.wireOp",EDGE,"E2.left"),sQuery(id+"F4.wireOp",EDGE,"E2.right")])],"isStart":false});
            extrude(context, id + "F25", {"entities" : qUnion([Q0]), "operationType" : NewBodyOperationType.REMOVE, "oppositeDirection" : true, "depth" : 200 * mm, "offsetDistance" : 25 * mm});
        }
        {
            var Q0;
            Q0=makeQuery(id+"F25.boolean.opBoolean","COPY",EDGE,{"derivedFrom":makeQuery(id+"F25.opExtrude","CAP_EDGE",EDGE,{"disambiguationData":[OSD([sQuery(id+"F0.wireOp",EDGE,"E0.bottom"),sQuery(id+"F0.wireOp",EDGE,"E0.left"),sQuery(id+"F4.wireOp",EDGE,"E2.bottom"),sQuery(id+"F4.wireOp",EDGE,"E2.left"),sQuery(id+"F4.wireOp",EDGE,"E2.right")])],"isStart":false})});
            var Q1;
            {var subQ0=sQuery(id+"F4.wireOp",EDGE,"E2.left");Q1=makeQuery(id+"F22.boolean.opBoolean","MERGE",EDGE,{"derivedFrom":[makeQuery(id+"F20.opExtrude","CAP_EDGE",EDGE,{"disambiguationData":[OSD([sQuery(id+"F0.wireOp",EDGE,"E0.bottom"),sQuery(id+"F0.wireOp",EDGE,"E0.left"),sQuery(id+"F4.wireOp",EDGE,"E2.top"),subQ0,sQuery(id+"F6.wireOp",EDGE,"E3.top"),sQuery(id+"F6.wireOp",EDGE,"E3.left")])],"isStart":false}),makeQuery(id+"F22.opExtrude","SWEPT_EDGE",EDGE,{"disambiguationData":[OSD([sQuery(id+"F4.wireOp",EDGE,"E2.bottom"),subQ0])]})]});}
            var Q2;
            {var subQ0=sQuery(id+"F6.wireOp",EDGE,"E3.bottom");Q2=makeQuery(id+"F20.boolean.opBoolean","MERGE",EDGE,{"derivedFrom":[makeQuery(id+"F19.boolean.opBoolean","COPY",EDGE,{"derivedFrom":makeQuery(id+"F19.opExtrude","CAP_EDGE",EDGE,{"disambiguationData":[OSD([sQuery(id+"F0.wireOp",EDGE,"E0.bottom"),sQuery(id+"F0.wireOp",EDGE,"E0.left"),subQ0,sQuery(id+"F6.wireOp",EDGE,"E3.right")])],"isStart":false})}),makeQuery(id+"F20.opExtrude","SWEPT_EDGE",EDGE,{"disambiguationData":[OSD([subQ0,sQuery(id+"F6.wireOp",EDGE,"E3.left")])]})]});}
            var Q3;
            Q3=makeQuery(id+"F19.boolean.opBoolean","COPY",EDGE,{"derivedFrom":makeQuery(id+"F19.opExtrude","CAP_EDGE",EDGE,{"disambiguationData":[OSD([sQuery(id+"F0.wireOp",EDGE,"E0.bottom"),sQuery(id+"F0.wireOp",EDGE,"E0.left"),sQuery(id+"F6.wireOp",EDGE,"E4.bottom"),sQuery(id+"F6.wireOp",EDGE,"E4.right")])],"isStart":false})});
            var Q4;
            {var subQ0=sQuery(id+"F4.wireOp",EDGE,"E1.left");var subQ1=sQuery(id+"F0.wireOp",EDGE,"E0.left");var subQ2=sQuery(id+"F0.wireOp",EDGE,"E0.bottom");Q4=makeQuery(id+"F22.boolean.opBoolean","MERGE",EDGE,{"derivedFrom":[makeQuery(id+"F19.boolean.opBoolean","MERGE",EDGE,{"derivedFrom":[makeQuery(id+"F3.boolean.opBoolean","MERGE",EDGE,{"derivedFrom":[makeQuery(id+"F1.opExtrude","CAP_EDGE",EDGE,{"disambiguationData":[OSD([subQ1])],"isStart":false}),makeQuery(id+"F3.opExtrude","SWEPT_EDGE",EDGE,{"disambiguationData":[OSD([subQ2,subQ1]),TDD([makeQuery(id+"F1.opExtrude","CAP_VERTEX",VERTEX,{"disambiguationData":[OSD([subQ2,subQ1])],"isStart":false})])]})]}),makeQuery(id+"F19.opExtrude","CAP_EDGE",EDGE,{"disambiguationData":[OSD([subQ2,subQ1,sQuery(id+"F6.wireOp",EDGE,"E4.top"),sQuery(id+"F6.wireOp",EDGE,"E4.left")])],"isStart":false}),makeQuery(id+"F19.opExtrude","CAP_EDGE",EDGE,{"disambiguationData":[OSD([subQ2,subQ1,sQuery(id+"F4.wireOp",EDGE,"E1.top"),subQ0])],"isStart":false})]}),makeQuery(id+"F22.opExtrude","SWEPT_EDGE",EDGE,{"disambiguationData":[OSD([sQuery(id+"F4.wireOp",EDGE,"E1.bottom"),subQ0])]})]});}
            var Q5;
            {var subQ0=sQuery(id+"F4.wireOp",EDGE,"E1.right");var subQ1=sQuery(id+"F4.wireOp",EDGE,"E1.bottom");var subQ2=sQuery(id+"F0.wireOp",EDGE,"E0.left");var subQ3=sQuery(id+"F0.wireOp",EDGE,"E0.bottom");Q5=makeQuery(id+"F25.boolean.opBoolean","COPY",EDGE,{"derivedFrom":makeQuery(id+"F25.opExtrude","CAP_EDGE",EDGE,{"disambiguationData":[OSD([subQ3,subQ2,subQ1,subQ0]),TDD([makeQuery(id+"F22.opExtrude","CAP_EDGE",EDGE,{"disambiguationData":[OSD([subQ3,subQ2,subQ1,subQ0]),TDD([makeQuery(id+"F19.boolean.opBoolean","COPY",EDGE,{"derivedFrom":makeQuery(id+"F19.opExtrude","CAP_EDGE",EDGE,{"disambiguationData":[OSD([subQ3,subQ2,subQ1,subQ0])],"isStart":false})})])],"isStart":false})])],"isStart":false})});}
            var Q6;
            {var subQ0=sQuery(id+"F0.wireOp",EDGE,"E0.left");var subQ1=sQuery(id+"F0.wireOp",EDGE,"E0.bottom");Q6=makeQuery(id+"F22.boolean.opBoolean","MERGE",FACE,{"derivedFrom":[makeQuery(id+"F20.boolean.opBoolean","MERGE",FACE,{"derivedFrom":[makeQuery(id+"F3.boolean.opBoolean","MERGE",FACE,{"derivedFrom":[makeQuery(id+"F2.boolean.opBoolean","MERGE",FACE,{"derivedFrom":[makeQuery(id+"F1.opExtrude","CAP_FACE",FACE,{"disambiguationData":[OSD([subQ1,sQuery(id+"F0.wireOp",EDGE,"E0.top"),subQ0,sQuery(id+"F0.wireOp",EDGE,"E0.right")])],"isStart":true}),makeQuery(id+"F2.opExtrude","SWEPT_FACE",FACE,{"disambiguationData":[OSD([subQ0]),TDD([makeQuery(id+"F1.opExtrude","CAP_EDGE",EDGE,{"disambiguationData":[OSD([subQ0])],"isStart":true})])]})]}),makeQuery(id+"F3.opExtrude","SWEPT_FACE",FACE,{"disambiguationData":[OSD([subQ1,subQ0]),TDD([makeQuery(id+"F2.boolean.opBoolean","MERGE",EDGE,{"derivedFrom":[makeQuery(id+"F1.opExtrude","CAP_EDGE",EDGE,{"disambiguationData":[OSD([subQ1])],"isStart":true}),makeQuery(id+"F2.opExtrude","SWEPT_EDGE",EDGE,{"disambiguationData":[OSD([subQ1,subQ0]),TDD([makeQuery(id+"F1.opExtrude","CAP_VERTEX",VERTEX,{"disambiguationData":[OSD([subQ1,subQ0])],"isStart":true})])]})]})])]})]}),makeQuery(id+"F20.opExtrude","SWEPT_FACE",FACE,{"disambiguationData":[OSD([subQ1,subQ0])]})]}),makeQuery(id+"F22.opExtrude","SWEPT_FACE",FACE,{"disambiguationData":[OSD([subQ1,subQ0])]})]});}
            chamfer(context, id + "F26", {"entities" : qUnion([Q0, Q1, Q2, Q3, Q4, Q5, Q6]), "width" : 1 * mm, "tangentPropagation" : true});
        }
    });
